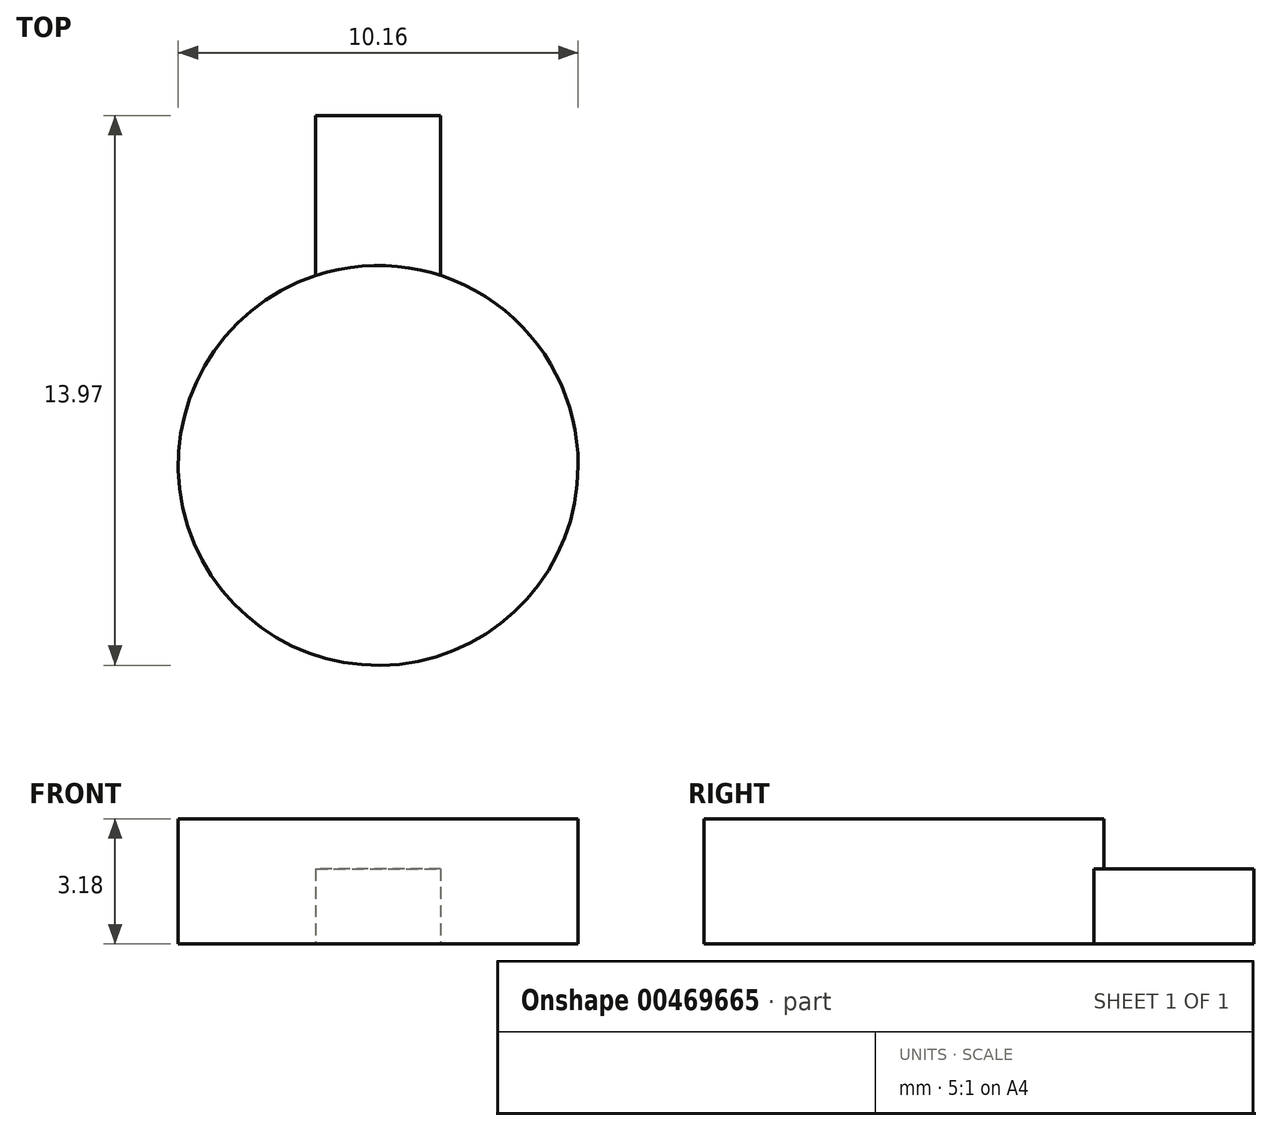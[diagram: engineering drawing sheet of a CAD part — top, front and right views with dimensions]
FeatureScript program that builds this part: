
annotation { "Feature Type Name" : "Feature", "Feature Type Description" : "" }
export const myFeature = defineFeature(function(context is Context, id is Id, definition is map)
    precondition{}
    {
        {
            var Q0;
            Q0=qCreatedBy(makeId("Top.planeOp"),FACE);
            var sketch = newSketch(context, id + "F0", { "sketchPlane" : qUnion([Q0])});
            skCircle(sketch, "E0", {"center": v(0, 0) * mm, "radius": 5.08 * mm});
            skLineSegment(sketch, "E1.top", {"start": v(-1.59, 8.9) * mm, "end": v(1.59, 8.9) * mm});
            skLineSegment(sketch, "E1.left", {"start": v(-1.59, 4.83) * mm, "end": v(-1.59, 8.9) * mm});
            skLineSegment(sketch, "E1.right", {"start": v(1.59, 4.83) * mm, "end": v(1.59, 8.9) * mm});
            skSolve(sketch);
        }
        {
            var Q0;
            {var subQ0=sQuery(id+"F0.wireOp",EDGE,"E0");var subQ1=makeQuery(id+"F0.imprint","INTERSECT",VERTEX,{"derivedFrom":[subQ0,sQuery(id+"F0.wireOp",EDGE,"E1.left")]});Q0=makeQuery(id+"F0.imprint","IMPRINT",FACE,{"disambiguationData":[TD([[makeQuery(id+"F0.imprint","IMPRINT",EDGE,{"disambiguationData":[TD([[subQ1,1.0]])],"derivedFrom":subQ0}),1.0]])]});}
            extrude(context, id + "F1", {"entities" : qUnion([Q0]), "depth" : 3.17 * mm});
        }
        {
            var Q0;
            Q0=makeQuery(id+"F0.imprint","IMPRINT",FACE,{"disambiguationData":[TD([[makeQuery(id+"F0.imprint","IMPRINT",EDGE,{"derivedFrom":sQuery(id+"F0.wireOp",EDGE,"E1.top")}),-1.0]])]});
            extrude(context, id + "F2", {"entities" : qUnion([Q0]), "operationType" : NewBodyOperationType.ADD, "depth" : 1.9 * mm});
        }
    });
